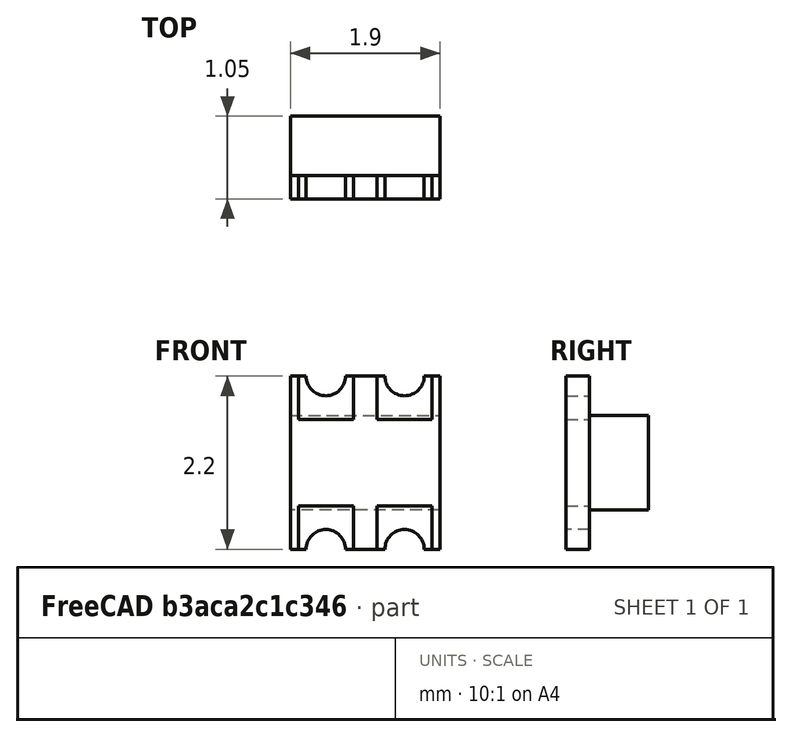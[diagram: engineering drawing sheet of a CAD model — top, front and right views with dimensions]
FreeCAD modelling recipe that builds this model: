
FCSTD DOCUMENT  (FreeCAD 0.18R16131 (Git))
Label: ws2812-2020
License: All rights reserved
LicenseURL: http://en.wikipedia.org/wiki/All_rights_reserved
objects: Sketcher::SketchObject×6, PartDesign::Pad×6, PartDesign::Body×6, Mesh::Feature×1
note: 24 computed .brp shape members not serialized (recipe doc carries the construction recipe); baked Part::Feature solids carry a one-line shape summary decoded from their .brp

FEATURE [Mesh::Feature] WS2812_2020  label="WS2812-2020"
  Placement = pos=(-0.95,0,1.1) rot=(0,0,1;0rad)
FEATURE [Sketcher::SketchObject] Sketch
  MapMode = 5
  Placement = pos=(0,0,0) rot=(1,0,0;1.5708rad)
  Support = -> [XZ_Plane]
  sketch-geometry (25):
    g0: LineSegment [constr] StartX=-0.95 StartY=1.1 StartZ=0 EndX=0.95 EndY=1.1 EndZ=0
    g1: LineSegment StartX=0.95 StartY=1.1 StartZ=0 EndX=0.95 EndY=-1.1 EndZ=0
    g2: LineSegment [constr] StartX=0.95 StartY=-1.1 StartZ=0 EndX=-0.95 EndY=-1.1 EndZ=0
    g3: LineSegment StartX=-0.95 StartY=-1.1 StartZ=0 EndX=-0.95 EndY=1.1 EndZ=0
    g4: LineSegment [constr] StartX=-0.95 StartY=1.1 StartZ=0 EndX=0 EndY=0 EndZ=0
    g5: LineSegment [constr] StartX=0 StartY=0 StartZ=0 EndX=0.95 EndY=1.1 EndZ=0
    g6: LineSegment [constr] StartX=0 StartY=0 StartZ=0 EndX=-0.95 EndY=-1.1 EndZ=0
    g7: LineSegment StartX=-0.95 StartY=1.1 StartZ=0 EndX=-0.85 EndY=1.1 EndZ=0
    g8: LineSegment StartX=-0.85 StartY=1.1 StartZ=0 EndX=-0.85 EndY=0.55 EndZ=0
    g9: LineSegment StartX=-0.85 StartY=0.55 StartZ=0 EndX=-0.15 EndY=0.55 EndZ=0
    g10: LineSegment StartX=-0.15 StartY=0.55 StartZ=0 EndX=-0.15 EndY=1.1 EndZ=0
    g11: LineSegment StartX=-0.15 StartY=1.1 StartZ=0 EndX=0.15 EndY=1.1 EndZ=0
    g12: LineSegment StartX=0.15 StartY=1.1 StartZ=0 EndX=0.15 EndY=0.55 EndZ=0
    g13: LineSegment StartX=0.15 StartY=0.55 StartZ=0 EndX=0.85 EndY=0.55 EndZ=0
    g14: LineSegment StartX=0.85 StartY=0.55 StartZ=0 EndX=0.85 EndY=1.1 EndZ=0
    g15: LineSegment StartX=0.85 StartY=1.1 StartZ=0 EndX=0.95 EndY=1.1 EndZ=0
    g16: LineSegment StartX=-0.95 StartY=-1.1 StartZ=0 EndX=-0.85 EndY=-1.1 EndZ=0
    g17: LineSegment StartX=-0.85 StartY=-1.1 StartZ=0 EndX=-0.85 EndY=-0.55 EndZ=0
    g18: LineSegment StartX=-0.85 StartY=-0.55 StartZ=0 EndX=-0.15 EndY=-0.55 EndZ=0
    g19: LineSegment StartX=-0.15 StartY=-0.55 StartZ=0 EndX=-0.15 EndY=-1.1 EndZ=0
    g20: LineSegment StartX=-0.15 StartY=-1.1 StartZ=0 EndX=0.15 EndY=-1.1 EndZ=0
    g21: LineSegment StartX=0.15 StartY=-1.1 StartZ=0 EndX=0.15 EndY=-0.55 EndZ=0
    g22: LineSegment StartX=0.15 StartY=-0.55 StartZ=0 EndX=0.85 EndY=-0.55 EndZ=0
    g23: LineSegment StartX=0.85 StartY=-0.55 StartZ=0 EndX=0.85 EndY=-1.1 EndZ=0
    g24: LineSegment StartX=0.85 StartY=-1.1 StartZ=0 EndX=0.95 EndY=-1.1 EndZ=0
  constraints (70):
    c: Coincident(g0,g1)
    c: Coincident(g1,g2)
    c: Coincident(g2,g3)
    c: Coincident(g3,g0)
    c: Horizontal(g0)
    c: Horizontal(g2)
    c: Vertical(g1)
    c: Vertical(g3)
    c: Coincident(g4,g0)
    c: Coincident(g4,g-1)
    c: Coincident(g5,g-1)
    c: Coincident(g5,g0)
    c: Coincident(g6,g-1)
    c: Coincident(g6,g2)
    c: Equal(g6,g4)
    c: Equal(g4,g5)
    c: DistanceX(g0,g0) = 1.9
    c: DistanceY(g3,g3) = 2.2
    c: Coincident(g7,g3)
    c: PointOnObject(g7,g0)
    c: Coincident(g7,g8)
    c: Vertical(g8)
    c: Coincident(g8,g9)
    c: Horizontal(g9)
    c: Coincident(g9,g10)
    c: Vertical(g10)
    c: Coincident(g10,g11)
    c: Coincident(g11,g12)
    c: Vertical(g12)
    c: Coincident(g12,g13)
    c: Horizontal(g13)
    c: Coincident(g13,g14)
    c: Vertical(g14)
    c: Coincident(g14,g15)
    c: Coincident(g15,g1)
    c: PointOnObject(g14,g0)
    c: PointOnObject(g11,g0)
    c: PointOnObject(g10,g0)
    c: Equal(g10,g12)
    c: Equal(g7,g15)
    c: DistanceX(g7,g7) = 0.1
    c: DistanceX(g11,g11) = 0.3
    c: DistanceY(g8,g8) = 0.55
    c: Equal(g9,g13)
    c: Coincident(g16,g3)
    c: Coincident(g16,g17)
    c: Coincident(g17,g18)
    c: Horizontal(g18)
    c: Coincident(g18,g19)
    c: Vertical(g19)
    c: Coincident(g19,g20)
    c: Coincident(g20,g21)
    c: Vertical(g21)
    c: Coincident(g21,g22)
    c: Horizontal(g22)
    c: Coincident(g22,g23)
    c: Vertical(g23)
    c: Coincident(g23,g24)
    c: Coincident(g24,g1)
    c: PointOnObject(g23,g2)
    c: PointOnObject(g20,g2)
    c: PointOnObject(g19,g2)
    c: PointOnObject(g16,g2)
    c: Vertical(g17)
    c: Equal(g16,g24)
    c: Equal(g24,g7)
    c: Equal(g20,g11)
    c: Equal(g9,g18)
    c: Equal(g21,g19)
    c: Equal(g19,g8)
FEATURE [PartDesign::Pad] Pad
  Length = 0.3
  Length2 = 100
  Placement = pos=(0,0,0) rot=(1,0,0;1.5708rad)
  Profile = -> Sketch
  Reversed = true
  Type = 0
FEATURE [PartDesign::Body] Body
  Group = -> [Sketch,Pad]
  Origin = -> Origin
  Tip = -> Pad
FEATURE [Sketcher::SketchObject] Sketch001
  MapMode = 5
  Placement = pos=(0,0,0) rot=(1,0,0;1.5708rad)
  Support = -> [XZ_Plane001]
  sketch-geometry (7):
    g0: LineSegment StartX=-0.95 StartY=0.6 StartZ=0 EndX=0.95 EndY=0.6 EndZ=0
    g1: LineSegment StartX=0.95 StartY=0.6 StartZ=0 EndX=0.95 EndY=-0.6 EndZ=0
    g2: LineSegment StartX=0.95 StartY=-0.6 StartZ=0 EndX=-0.95 EndY=-0.6 EndZ=0
    g3: LineSegment StartX=-0.95 StartY=-0.6 StartZ=0 EndX=-0.95 EndY=0.6 EndZ=0
    g4: LineSegment [constr] StartX=-0.95 StartY=0.6 StartZ=0 EndX=0 EndY=0 EndZ=0
    g5: LineSegment [constr] StartX=0 StartY=0 StartZ=0 EndX=0.95 EndY=0.6 EndZ=0
    g6: LineSegment [constr] StartX=0 StartY=0 StartZ=0 EndX=-0.95 EndY=-0.6 EndZ=0
  constraints (18):
    c: Coincident(g0,g1)
    c: Coincident(g1,g2)
    c: Coincident(g2,g3)
    c: Coincident(g3,g0)
    c: Horizontal(g0)
    c: Horizontal(g2)
    c: Vertical(g1)
    c: Vertical(g3)
    c: Coincident(g4,g0)
    c: Coincident(g4,g-1)
    c: Coincident(g5,g-1)
    c: Coincident(g5,g0)
    c: Coincident(g6,g-1)
    c: Coincident(g6,g2)
    c: Equal(g6,g4)
    c: Equal(g4,g5)
    c: DistanceX(g0,g0) = 1.9
    c: DistanceY(g3,g3) = 1.2
FEATURE [PartDesign::Pad] Pad001
  Length = 0.75
  Length2 = 100
  Placement = pos=(0,0,0) rot=(1,0,0;1.5708rad)
  Profile = -> Sketch001
  Reversed = true
  Type = 0
FEATURE [PartDesign::Body] Body001
  Group = -> [Sketch001,Pad001]
  Origin = -> Origin001
  Placement = pos=(0,0.3,0) rot=(0,0,1;0rad)
  Tip = -> Pad001
FEATURE [Sketcher::SketchObject] Sketch002
  MapMode = 5
  Placement = pos=(0,0,0) rot=(1,0,0;1.5708rad)
  Support = -> [XZ_Plane002]
  sketch-geometry (28):
    g0: LineSegment [constr] StartX=-0.95 StartY=1.1 StartZ=0 EndX=0.95 EndY=1.1 EndZ=0
    g1: LineSegment [constr] StartX=0.95 StartY=1.1 StartZ=0 EndX=0.95 EndY=-1.1 EndZ=0
    g2: LineSegment [constr] StartX=0.95 StartY=-1.1 StartZ=0 EndX=-0.95 EndY=-1.1 EndZ=0
    g3: LineSegment [constr] StartX=-0.95 StartY=-1.1 StartZ=0 EndX=-0.95 EndY=1.1 EndZ=0
    g4: LineSegment [constr] StartX=-0.95 StartY=1.1 StartZ=0 EndX=0 EndY=0 EndZ=0
    g5: LineSegment [constr] StartX=0 StartY=0 StartZ=0 EndX=0.95 EndY=1.1 EndZ=0
    g6: LineSegment [constr] StartX=0 StartY=0 StartZ=0 EndX=-0.95 EndY=-1.1 EndZ=0
    g7: LineSegment [constr] StartX=-0.95 StartY=1.1 StartZ=0 EndX=-0.85 EndY=1.1 EndZ=0
    g8: LineSegment StartX=-0.85 StartY=1.1 StartZ=0 EndX=-0.85 EndY=0.55 EndZ=0
    g9: LineSegment StartX=-0.85 StartY=0.55 StartZ=0 EndX=-0.15 EndY=0.55 EndZ=0
    g10: LineSegment StartX=-0.15 StartY=0.55 StartZ=0 EndX=-0.15 EndY=1.1 EndZ=0
    g11: LineSegment [constr] StartX=-0.15 StartY=1.1 StartZ=0 EndX=0.15 EndY=1.1 EndZ=0
    g12: LineSegment [constr] StartX=0.15 StartY=1.1 StartZ=0 EndX=0.15 EndY=0.55 EndZ=0
    g13: LineSegment [constr] StartX=0.15 StartY=0.55 StartZ=0 EndX=0.85 EndY=0.55 EndZ=0
    g14: LineSegment [constr] StartX=0.85 StartY=0.55 StartZ=0 EndX=0.85 EndY=1.1 EndZ=0
    g15: LineSegment [constr] StartX=0.85 StartY=1.1 StartZ=0 EndX=0.95 EndY=1.1 EndZ=0
    g16: LineSegment [constr] StartX=-0.95 StartY=-1.1 StartZ=0 EndX=-0.85 EndY=-1.1 EndZ=0
    g17: LineSegment [constr] StartX=-0.85 StartY=-1.1 StartZ=0 EndX=-0.85 EndY=-0.55 EndZ=0
    g18: LineSegment [constr] StartX=-0.85 StartY=-0.55 StartZ=0 EndX=-0.15 EndY=-0.55 EndZ=0
    g19: LineSegment [constr] StartX=-0.15 StartY=-0.55 StartZ=0 EndX=-0.15 EndY=-1.1 EndZ=0
    g20: LineSegment [constr] StartX=-0.15 StartY=-1.1 StartZ=0 EndX=0.15 EndY=-1.1 EndZ=0
    g21: LineSegment [constr] StartX=0.15 StartY=-1.1 StartZ=0 EndX=0.15 EndY=-0.55 EndZ=0
    g22: LineSegment [constr] StartX=0.15 StartY=-0.55 StartZ=0 EndX=0.85 EndY=-0.55 EndZ=0
    g23: LineSegment [constr] StartX=0.85 StartY=-0.55 StartZ=0 EndX=0.85 EndY=-1.1 EndZ=0
    g24: LineSegment [constr] StartX=0.85 StartY=-1.1 StartZ=0 EndX=0.95 EndY=-1.1 EndZ=0
    g25: LineSegment StartX=-0.85 StartY=1.1 StartZ=0 EndX=-0.75 EndY=1.1 EndZ=0
    g26: LineSegment StartX=-0.15 StartY=1.1 StartZ=0 EndX=-0.25 EndY=1.1 EndZ=0
    g27: ArcOfCircle CenterX=-0.5 CenterY=1.1 CenterZ=0 NormalX=0 NormalY=0 NormalZ=1 AngleXU=0 Radius=0.25 StartAngle=3.14159 EndAngle=6.28319
  constraints (79):
    c: Coincident(g0,g1)
    c: Coincident(g1,g2)
    c: Coincident(g2,g3)
    c: Coincident(g3,g0)
    c: Horizontal(g0)
    c: Horizontal(g2)
    c: Vertical(g1)
    c: Vertical(g3)
    c: Coincident(g4,g0)
    c: Coincident(g4,g-1)
    c: Coincident(g5,g-1)
    c: Coincident(g5,g0)
    c: Coincident(g6,g-1)
    c: Coincident(g6,g2)
    c: Equal(g6,g4)
    c: Equal(g4,g5)
    c: DistanceX(g0,g0) = 1.9
    c: DistanceY(g3,g3) = 2.2
    c: Coincident(g7,g3)
    c: PointOnObject(g7,g0)
    c: Coincident(g7,g8)
    c: Vertical(g8)
    c: Coincident(g8,g9)
    c: Horizontal(g9)
    c: Coincident(g9,g10)
    c: Vertical(g10)
    c: Coincident(g10,g11)
    c: Coincident(g11,g12)
    c: Vertical(g12)
    c: Coincident(g12,g13)
    c: Horizontal(g13)
    c: Coincident(g13,g14)
    c: Vertical(g14)
    c: Coincident(g14,g15)
    c: Coincident(g15,g1)
    c: PointOnObject(g14,g0)
    c: PointOnObject(g11,g0)
    c: PointOnObject(g10,g0)
    c: Equal(g10,g12)
    c: Equal(g7,g15)
    c: DistanceX(g7,g7) = 0.1
    c: DistanceX(g11,g11) = 0.3
    c: DistanceY(g8,g8) = 0.55
    c: Equal(g9,g13)
    c: Coincident(g16,g3)
    c: Coincident(g16,g17)
    c: Coincident(g17,g18)
    c: Horizontal(g18)
    c: Coincident(g18,g19)
    c: Vertical(g19)
    c: Coincident(g19,g20)
    c: Coincident(g20,g21)
    c: Vertical(g21)
    c: Coincident(g21,g22)
    c: Horizontal(g22)
    c: Coincident(g22,g23)
    c: Vertical(g23)
    c: Coincident(g23,g24)
    c: Coincident(g24,g1)
    c: PointOnObject(g23,g2)
    c: PointOnObject(g20,g2)
    c: PointOnObject(g19,g2)
    c: PointOnObject(g16,g2)
    c: Vertical(g17)
    c: Equal(g16,g24)
    c: Equal(g24,g7)
    c: Equal(g20,g11)
    c: Equal(g9,g18)
    c: Equal(g21,g19)
    c: Equal(g19,g8)
    c: Coincident(g25,g8)
    c: Coincident(g26,g10)
    c: PointOnObject(g26,g0)
    c: PointOnObject(g25,g0)
    c: Equal(g26,g25)
    c: PointOnObject(g27,g0)
    c: Coincident(g27,g25)
    c: Coincident(g27,g26)
    c: DistanceX(g25,g26) = 0.5
FEATURE [PartDesign::Pad] Pad002
  Length = 0.3
  Length2 = 100
  Placement = pos=(0,0,0) rot=(1,0,0;1.5708rad)
  Profile = -> Sketch002
  Reversed = true
  Type = 0
FEATURE [PartDesign::Body] Body002  label="LEG"
  Group = -> [Sketch002,Pad002]
  Origin = -> Origin002
  Tip = -> Pad002
FEATURE [Sketcher::SketchObject] Sketch003
  MapMode = 5
  Placement = pos=(0,0,0) rot=(1,0,0;1.5708rad)
  Support = -> [XZ_Plane003]
  sketch-geometry (28):
    g0: LineSegment [constr] StartX=-0.95 StartY=1.1 StartZ=0 EndX=0.95 EndY=1.1 EndZ=0
    g1: LineSegment [constr] StartX=0.95 StartY=1.1 StartZ=0 EndX=0.95 EndY=-1.1 EndZ=0
    g2: LineSegment [constr] StartX=0.95 StartY=-1.1 StartZ=0 EndX=-0.95 EndY=-1.1 EndZ=0
    g3: LineSegment [constr] StartX=-0.95 StartY=-1.1 StartZ=0 EndX=-0.95 EndY=1.1 EndZ=0
    g4: LineSegment [constr] StartX=-0.95 StartY=1.1 StartZ=0 EndX=0 EndY=0 EndZ=0
    g5: LineSegment [constr] StartX=0 StartY=0 StartZ=0 EndX=0.95 EndY=1.1 EndZ=0
    g6: LineSegment [constr] StartX=0 StartY=0 StartZ=0 EndX=-0.95 EndY=-1.1 EndZ=0
    g7: LineSegment [constr] StartX=-0.95 StartY=1.1 StartZ=0 EndX=-0.85 EndY=1.1 EndZ=0
    g8: LineSegment StartX=-0.85 StartY=1.1 StartZ=0 EndX=-0.85 EndY=0.55 EndZ=0
    g9: LineSegment StartX=-0.85 StartY=0.55 StartZ=0 EndX=-0.15 EndY=0.55 EndZ=0
    g10: LineSegment StartX=-0.15 StartY=0.55 StartZ=0 EndX=-0.15 EndY=1.1 EndZ=0
    g11: LineSegment [constr] StartX=-0.15 StartY=1.1 StartZ=0 EndX=0.15 EndY=1.1 EndZ=0
    g12: LineSegment [constr] StartX=0.15 StartY=1.1 StartZ=0 EndX=0.15 EndY=0.55 EndZ=0
    g13: LineSegment [constr] StartX=0.15 StartY=0.55 StartZ=0 EndX=0.85 EndY=0.55 EndZ=0
    g14: LineSegment [constr] StartX=0.85 StartY=0.55 StartZ=0 EndX=0.85 EndY=1.1 EndZ=0
    g15: LineSegment [constr] StartX=0.85 StartY=1.1 StartZ=0 EndX=0.95 EndY=1.1 EndZ=0
    g16: LineSegment [constr] StartX=-0.95 StartY=-1.1 StartZ=0 EndX=-0.85 EndY=-1.1 EndZ=0
    g17: LineSegment [constr] StartX=-0.85 StartY=-1.1 StartZ=0 EndX=-0.85 EndY=-0.55 EndZ=0
    g18: LineSegment [constr] StartX=-0.85 StartY=-0.55 StartZ=0 EndX=-0.15 EndY=-0.55 EndZ=0
    g19: LineSegment [constr] StartX=-0.15 StartY=-0.55 StartZ=0 EndX=-0.15 EndY=-1.1 EndZ=0
    g20: LineSegment [constr] StartX=-0.15 StartY=-1.1 StartZ=0 EndX=0.15 EndY=-1.1 EndZ=0
    g21: LineSegment [constr] StartX=0.15 StartY=-1.1 StartZ=0 EndX=0.15 EndY=-0.55 EndZ=0
    g22: LineSegment [constr] StartX=0.15 StartY=-0.55 StartZ=0 EndX=0.85 EndY=-0.55 EndZ=0
    g23: LineSegment [constr] StartX=0.85 StartY=-0.55 StartZ=0 EndX=0.85 EndY=-1.1 EndZ=0
    g24: LineSegment [constr] StartX=0.85 StartY=-1.1 StartZ=0 EndX=0.95 EndY=-1.1 EndZ=0
    g25: LineSegment StartX=-0.85 StartY=1.1 StartZ=0 EndX=-0.75 EndY=1.1 EndZ=0
    g26: LineSegment StartX=-0.15 StartY=1.1 StartZ=0 EndX=-0.25 EndY=1.1 EndZ=0
    g27: ArcOfCircle CenterX=-0.5 CenterY=1.1 CenterZ=0 NormalX=0 NormalY=0 NormalZ=1 AngleXU=0 Radius=0.25 StartAngle=3.14159 EndAngle=6.28319
  constraints (79):
    c: Coincident(g0,g1)
    c: Coincident(g1,g2)
    c: Coincident(g2,g3)
    c: Coincident(g3,g0)
    c: Horizontal(g0)
    c: Horizontal(g2)
    c: Vertical(g1)
    c: Vertical(g3)
    c: Coincident(g4,g0)
    c: Coincident(g4,g-1)
    c: Coincident(g5,g-1)
    c: Coincident(g5,g0)
    c: Coincident(g6,g-1)
    c: Coincident(g6,g2)
    c: Equal(g6,g4)
    c: Equal(g4,g5)
    c: DistanceX(g0,g0) = 1.9
    c: DistanceY(g3,g3) = 2.2
    c: Coincident(g7,g3)
    c: PointOnObject(g7,g0)
    c: Coincident(g7,g8)
    c: Vertical(g8)
    c: Coincident(g8,g9)
    c: Horizontal(g9)
    c: Coincident(g9,g10)
    c: Vertical(g10)
    c: Coincident(g10,g11)
    c: Coincident(g11,g12)
    c: Vertical(g12)
    c: Coincident(g12,g13)
    c: Horizontal(g13)
    c: Coincident(g13,g14)
    c: Vertical(g14)
    c: Coincident(g14,g15)
    c: Coincident(g15,g1)
    c: PointOnObject(g14,g0)
    c: PointOnObject(g11,g0)
    c: PointOnObject(g10,g0)
    c: Equal(g10,g12)
    c: Equal(g7,g15)
    c: DistanceX(g7,g7) = 0.1
    c: DistanceX(g11,g11) = 0.3
    c: DistanceY(g8,g8) = 0.55
    c: Equal(g9,g13)
    c: Coincident(g16,g3)
    c: Coincident(g16,g17)
    c: Coincident(g17,g18)
    c: Horizontal(g18)
    c: Coincident(g18,g19)
    c: Vertical(g19)
    c: Coincident(g19,g20)
    c: Coincident(g20,g21)
    c: Vertical(g21)
    c: Coincident(g21,g22)
    c: Horizontal(g22)
    c: Coincident(g22,g23)
    c: Vertical(g23)
    c: Coincident(g23,g24)
    c: Coincident(g24,g1)
    c: PointOnObject(g23,g2)
    c: PointOnObject(g20,g2)
    c: PointOnObject(g19,g2)
    c: PointOnObject(g16,g2)
    c: Vertical(g17)
    c: Equal(g16,g24)
    c: Equal(g24,g7)
    c: Equal(g20,g11)
    c: Equal(g9,g18)
    c: Equal(g21,g19)
    c: Equal(g19,g8)
    c: Coincident(g25,g8)
    c: Coincident(g26,g10)
    c: PointOnObject(g26,g0)
    c: PointOnObject(g25,g0)
    c: Equal(g26,g25)
    c: PointOnObject(g27,g0)
    c: Coincident(g27,g25)
    c: Coincident(g27,g26)
    c: DistanceX(g25,g26) = 0.5
FEATURE [PartDesign::Pad] Pad003
  Length = 0.3
  Length2 = 100
  Placement = pos=(0,0,0) rot=(1,0,0;1.5708rad)
  Profile = -> Sketch003
  Reversed = true
  Type = 0
FEATURE [PartDesign::Body] Body003  label="LEG001"
  Group = -> [Sketch003,Pad003]
  Origin = -> Origin003
  Placement = pos=(0,0.3,0) rot=(0,0,1;3.14159rad)
  Tip = -> Pad003
FEATURE [Sketcher::SketchObject] Sketch004
  MapMode = 5
  Placement = pos=(0,0,0) rot=(1,0,0;1.5708rad)
  Support = -> [XZ_Plane004]
  sketch-geometry (28):
    g0: LineSegment [constr] StartX=-0.95 StartY=1.1 StartZ=0 EndX=0.95 EndY=1.1 EndZ=0
    g1: LineSegment [constr] StartX=0.95 StartY=1.1 StartZ=0 EndX=0.95 EndY=-1.1 EndZ=0
    g2: LineSegment [constr] StartX=0.95 StartY=-1.1 StartZ=0 EndX=-0.95 EndY=-1.1 EndZ=0
    g3: LineSegment [constr] StartX=-0.95 StartY=-1.1 StartZ=0 EndX=-0.95 EndY=1.1 EndZ=0
    g4: LineSegment [constr] StartX=-0.95 StartY=1.1 StartZ=0 EndX=0 EndY=0 EndZ=0
    g5: LineSegment [constr] StartX=0 StartY=0 StartZ=0 EndX=0.95 EndY=1.1 EndZ=0
    g6: LineSegment [constr] StartX=0 StartY=0 StartZ=0 EndX=-0.95 EndY=-1.1 EndZ=0
    g7: LineSegment [constr] StartX=-0.95 StartY=1.1 StartZ=0 EndX=-0.85 EndY=1.1 EndZ=0
    g8: LineSegment StartX=-0.85 StartY=1.1 StartZ=0 EndX=-0.85 EndY=0.55 EndZ=0
    g9: LineSegment StartX=-0.85 StartY=0.55 StartZ=0 EndX=-0.15 EndY=0.55 EndZ=0
    g10: LineSegment StartX=-0.15 StartY=0.55 StartZ=0 EndX=-0.15 EndY=1.1 EndZ=0
    g11: LineSegment [constr] StartX=-0.15 StartY=1.1 StartZ=0 EndX=0.15 EndY=1.1 EndZ=0
    g12: LineSegment [constr] StartX=0.15 StartY=1.1 StartZ=0 EndX=0.15 EndY=0.55 EndZ=0
    g13: LineSegment [constr] StartX=0.15 StartY=0.55 StartZ=0 EndX=0.85 EndY=0.55 EndZ=0
    g14: LineSegment [constr] StartX=0.85 StartY=0.55 StartZ=0 EndX=0.85 EndY=1.1 EndZ=0
    g15: LineSegment [constr] StartX=0.85 StartY=1.1 StartZ=0 EndX=0.95 EndY=1.1 EndZ=0
    g16: LineSegment [constr] StartX=-0.95 StartY=-1.1 StartZ=0 EndX=-0.85 EndY=-1.1 EndZ=0
    g17: LineSegment [constr] StartX=-0.85 StartY=-1.1 StartZ=0 EndX=-0.85 EndY=-0.55 EndZ=0
    g18: LineSegment [constr] StartX=-0.85 StartY=-0.55 StartZ=0 EndX=-0.15 EndY=-0.55 EndZ=0
    g19: LineSegment [constr] StartX=-0.15 StartY=-0.55 StartZ=0 EndX=-0.15 EndY=-1.1 EndZ=0
    g20: LineSegment [constr] StartX=-0.15 StartY=-1.1 StartZ=0 EndX=0.15 EndY=-1.1 EndZ=0
    g21: LineSegment [constr] StartX=0.15 StartY=-1.1 StartZ=0 EndX=0.15 EndY=-0.55 EndZ=0
    g22: LineSegment [constr] StartX=0.15 StartY=-0.55 StartZ=0 EndX=0.85 EndY=-0.55 EndZ=0
    g23: LineSegment [constr] StartX=0.85 StartY=-0.55 StartZ=0 EndX=0.85 EndY=-1.1 EndZ=0
    g24: LineSegment [constr] StartX=0.85 StartY=-1.1 StartZ=0 EndX=0.95 EndY=-1.1 EndZ=0
    g25: LineSegment StartX=-0.85 StartY=1.1 StartZ=0 EndX=-0.75 EndY=1.1 EndZ=0
    g26: LineSegment StartX=-0.15 StartY=1.1 StartZ=0 EndX=-0.25 EndY=1.1 EndZ=0
    g27: ArcOfCircle CenterX=-0.5 CenterY=1.1 CenterZ=0 NormalX=0 NormalY=0 NormalZ=1 AngleXU=0 Radius=0.25 StartAngle=3.14159 EndAngle=6.28319
  constraints (79):
    c: Coincident(g0,g1)
    c: Coincident(g1,g2)
    c: Coincident(g2,g3)
    c: Coincident(g3,g0)
    c: Horizontal(g0)
    c: Horizontal(g2)
    c: Vertical(g1)
    c: Vertical(g3)
    c: Coincident(g4,g0)
    c: Coincident(g4,g-1)
    c: Coincident(g5,g-1)
    c: Coincident(g5,g0)
    c: Coincident(g6,g-1)
    c: Coincident(g6,g2)
    c: Equal(g6,g4)
    c: Equal(g4,g5)
    c: DistanceX(g0,g0) = 1.9
    c: DistanceY(g3,g3) = 2.2
    c: Coincident(g7,g3)
    c: PointOnObject(g7,g0)
    c: Coincident(g7,g8)
    c: Vertical(g8)
    c: Coincident(g8,g9)
    c: Horizontal(g9)
    c: Coincident(g9,g10)
    c: Vertical(g10)
    c: Coincident(g10,g11)
    c: Coincident(g11,g12)
    c: Vertical(g12)
    c: Coincident(g12,g13)
    c: Horizontal(g13)
    c: Coincident(g13,g14)
    c: Vertical(g14)
    c: Coincident(g14,g15)
    c: Coincident(g15,g1)
    c: PointOnObject(g14,g0)
    c: PointOnObject(g11,g0)
    c: PointOnObject(g10,g0)
    c: Equal(g10,g12)
    c: Equal(g7,g15)
    c: DistanceX(g7,g7) = 0.1
    c: DistanceX(g11,g11) = 0.3
    c: DistanceY(g8,g8) = 0.55
    c: Equal(g9,g13)
    c: Coincident(g16,g3)
    c: Coincident(g16,g17)
    c: Coincident(g17,g18)
    c: Horizontal(g18)
    c: Coincident(g18,g19)
    c: Vertical(g19)
    c: Coincident(g19,g20)
    c: Coincident(g20,g21)
    c: Vertical(g21)
    c: Coincident(g21,g22)
    c: Horizontal(g22)
    c: Coincident(g22,g23)
    c: Vertical(g23)
    c: Coincident(g23,g24)
    c: Coincident(g24,g1)
    c: PointOnObject(g23,g2)
    c: PointOnObject(g20,g2)
    c: PointOnObject(g19,g2)
    c: PointOnObject(g16,g2)
    c: Vertical(g17)
    c: Equal(g16,g24)
    c: Equal(g24,g7)
    c: Equal(g20,g11)
    c: Equal(g9,g18)
    c: Equal(g21,g19)
    c: Equal(g19,g8)
    c: Coincident(g25,g8)
    c: Coincident(g26,g10)
    c: PointOnObject(g26,g0)
    c: PointOnObject(g25,g0)
    c: Equal(g26,g25)
    c: PointOnObject(g27,g0)
    c: Coincident(g27,g25)
    c: Coincident(g27,g26)
    c: DistanceX(g25,g26) = 0.5
FEATURE [PartDesign::Pad] Pad004
  Length = 0.3
  Length2 = 100
  Placement = pos=(0,0,0) rot=(1,0,0;1.5708rad)
  Profile = -> Sketch004
  Reversed = true
  Type = 0
FEATURE [PartDesign::Body] Body004  label="LEG002"
  Group = -> [Sketch004,Pad004]
  Origin = -> Origin004
  Placement = pos=(0,0,0) rot=(0,1,0;3.14159rad)
  Tip = -> Pad004
FEATURE [Sketcher::SketchObject] Sketch005
  MapMode = 5
  Placement = pos=(0,0,0) rot=(1,0,0;1.5708rad)
  Support = -> [XZ_Plane005]
  sketch-geometry (28):
    g0: LineSegment [constr] StartX=-0.95 StartY=1.1 StartZ=0 EndX=0.95 EndY=1.1 EndZ=0
    g1: LineSegment [constr] StartX=0.95 StartY=1.1 StartZ=0 EndX=0.95 EndY=-1.1 EndZ=0
    g2: LineSegment [constr] StartX=0.95 StartY=-1.1 StartZ=0 EndX=-0.95 EndY=-1.1 EndZ=0
    g3: LineSegment [constr] StartX=-0.95 StartY=-1.1 StartZ=0 EndX=-0.95 EndY=1.1 EndZ=0
    g4: LineSegment [constr] StartX=-0.95 StartY=1.1 StartZ=0 EndX=0 EndY=0 EndZ=0
    g5: LineSegment [constr] StartX=0 StartY=0 StartZ=0 EndX=0.95 EndY=1.1 EndZ=0
    g6: LineSegment [constr] StartX=0 StartY=0 StartZ=0 EndX=-0.95 EndY=-1.1 EndZ=0
    g7: LineSegment [constr] StartX=-0.95 StartY=1.1 StartZ=0 EndX=-0.85 EndY=1.1 EndZ=0
    g8: LineSegment StartX=-0.85 StartY=1.1 StartZ=0 EndX=-0.85 EndY=0.55 EndZ=0
    g9: LineSegment StartX=-0.85 StartY=0.55 StartZ=0 EndX=-0.15 EndY=0.55 EndZ=0
    g10: LineSegment StartX=-0.15 StartY=0.55 StartZ=0 EndX=-0.15 EndY=1.1 EndZ=0
    g11: LineSegment [constr] StartX=-0.15 StartY=1.1 StartZ=0 EndX=0.15 EndY=1.1 EndZ=0
    g12: LineSegment [constr] StartX=0.15 StartY=1.1 StartZ=0 EndX=0.15 EndY=0.55 EndZ=0
    g13: LineSegment [constr] StartX=0.15 StartY=0.55 StartZ=0 EndX=0.85 EndY=0.55 EndZ=0
    g14: LineSegment [constr] StartX=0.85 StartY=0.55 StartZ=0 EndX=0.85 EndY=1.1 EndZ=0
    g15: LineSegment [constr] StartX=0.85 StartY=1.1 StartZ=0 EndX=0.95 EndY=1.1 EndZ=0
    g16: LineSegment [constr] StartX=-0.95 StartY=-1.1 StartZ=0 EndX=-0.85 EndY=-1.1 EndZ=0
    g17: LineSegment [constr] StartX=-0.85 StartY=-1.1 StartZ=0 EndX=-0.85 EndY=-0.55 EndZ=0
    g18: LineSegment [constr] StartX=-0.85 StartY=-0.55 StartZ=0 EndX=-0.15 EndY=-0.55 EndZ=0
    g19: LineSegment [constr] StartX=-0.15 StartY=-0.55 StartZ=0 EndX=-0.15 EndY=-1.1 EndZ=0
    g20: LineSegment [constr] StartX=-0.15 StartY=-1.1 StartZ=0 EndX=0.15 EndY=-1.1 EndZ=0
    g21: LineSegment [constr] StartX=0.15 StartY=-1.1 StartZ=0 EndX=0.15 EndY=-0.55 EndZ=0
    g22: LineSegment [constr] StartX=0.15 StartY=-0.55 StartZ=0 EndX=0.85 EndY=-0.55 EndZ=0
    g23: LineSegment [constr] StartX=0.85 StartY=-0.55 StartZ=0 EndX=0.85 EndY=-1.1 EndZ=0
    g24: LineSegment [constr] StartX=0.85 StartY=-1.1 StartZ=0 EndX=0.95 EndY=-1.1 EndZ=0
    g25: LineSegment StartX=-0.85 StartY=1.1 StartZ=0 EndX=-0.75 EndY=1.1 EndZ=0
    g26: LineSegment StartX=-0.15 StartY=1.1 StartZ=0 EndX=-0.25 EndY=1.1 EndZ=0
    g27: ArcOfCircle CenterX=-0.5 CenterY=1.1 CenterZ=0 NormalX=0 NormalY=0 NormalZ=1 AngleXU=0 Radius=0.25 StartAngle=3.14159 EndAngle=6.28319
  constraints (79):
    c: Coincident(g0,g1)
    c: Coincident(g1,g2)
    c: Coincident(g2,g3)
    c: Coincident(g3,g0)
    c: Horizontal(g0)
    c: Horizontal(g2)
    c: Vertical(g1)
    c: Vertical(g3)
    c: Coincident(g4,g0)
    c: Coincident(g4,g-1)
    c: Coincident(g5,g-1)
    c: Coincident(g5,g0)
    c: Coincident(g6,g-1)
    c: Coincident(g6,g2)
    c: Equal(g6,g4)
    c: Equal(g4,g5)
    c: DistanceX(g0,g0) = 1.9
    c: DistanceY(g3,g3) = 2.2
    c: Coincident(g7,g3)
    c: PointOnObject(g7,g0)
    c: Coincident(g7,g8)
    c: Vertical(g8)
    c: Coincident(g8,g9)
    c: Horizontal(g9)
    c: Coincident(g9,g10)
    c: Vertical(g10)
    c: Coincident(g10,g11)
    c: Coincident(g11,g12)
    c: Vertical(g12)
    c: Coincident(g12,g13)
    c: Horizontal(g13)
    c: Coincident(g13,g14)
    c: Vertical(g14)
    c: Coincident(g14,g15)
    c: Coincident(g15,g1)
    c: PointOnObject(g14,g0)
    c: PointOnObject(g11,g0)
    c: PointOnObject(g10,g0)
    c: Equal(g10,g12)
    c: Equal(g7,g15)
    c: DistanceX(g7,g7) = 0.1
    c: DistanceX(g11,g11) = 0.3
    c: DistanceY(g8,g8) = 0.55
    c: Equal(g9,g13)
    c: Coincident(g16,g3)
    c: Coincident(g16,g17)
    c: Coincident(g17,g18)
    c: Horizontal(g18)
    c: Coincident(g18,g19)
    c: Vertical(g19)
    c: Coincident(g19,g20)
    c: Coincident(g20,g21)
    c: Vertical(g21)
    c: Coincident(g21,g22)
    c: Horizontal(g22)
    c: Coincident(g22,g23)
    c: Vertical(g23)
    c: Coincident(g23,g24)
    c: Coincident(g24,g1)
    c: PointOnObject(g23,g2)
    c: PointOnObject(g20,g2)
    c: PointOnObject(g19,g2)
    c: PointOnObject(g16,g2)
    c: Vertical(g17)
    c: Equal(g16,g24)
    c: Equal(g24,g7)
    c: Equal(g20,g11)
    c: Equal(g9,g18)
    c: Equal(g21,g19)
    c: Equal(g19,g8)
    c: Coincident(g25,g8)
    c: Coincident(g26,g10)
    c: PointOnObject(g26,g0)
    c: PointOnObject(g25,g0)
    c: Equal(g26,g25)
    c: PointOnObject(g27,g0)
    c: Coincident(g27,g25)
    c: Coincident(g27,g26)
    c: DistanceX(g25,g26) = 0.5
FEATURE [PartDesign::Pad] Pad005
  Length = 0.3
  Length2 = 100
  Placement = pos=(0,0,0) rot=(1,0,0;1.5708rad)
  Profile = -> Sketch005
  Reversed = true
  Type = 0
FEATURE [PartDesign::Body] Body005  label="LEG003"
  Group = -> [Sketch005,Pad005]
  Origin = -> Origin005
  Placement = pos=(0,0.3,0) rot=(1,0,0;3.14159rad)
  Tip = -> Pad005
